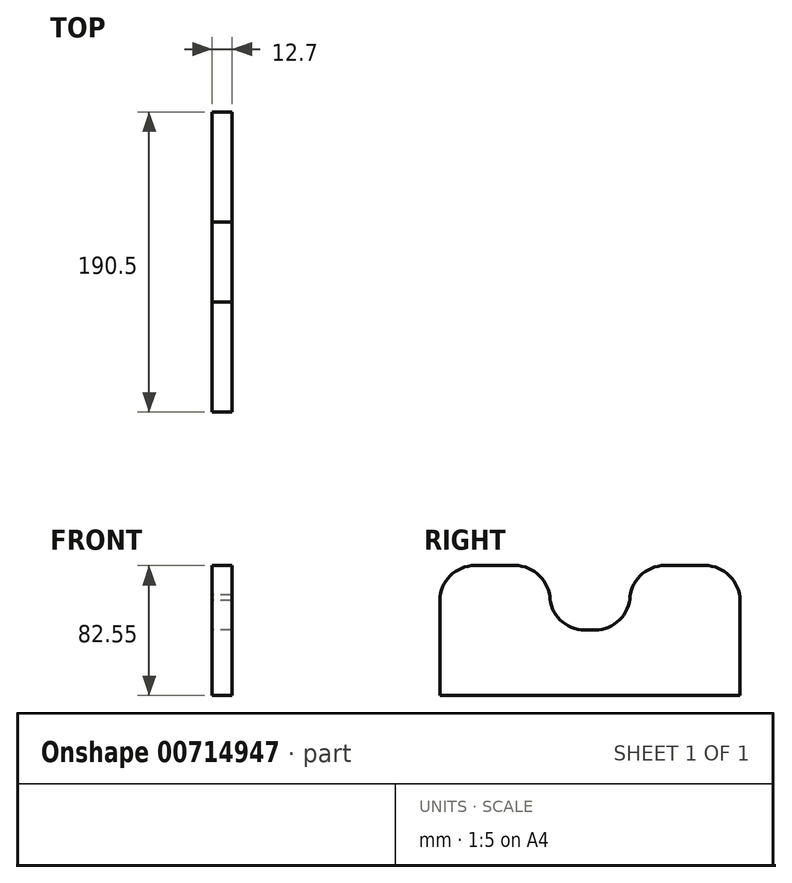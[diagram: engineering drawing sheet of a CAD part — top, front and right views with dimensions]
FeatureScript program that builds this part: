
annotation { "Feature Type Name" : "Feature", "Feature Type Description" : "" }
export const myFeature = defineFeature(function(context is Context, id is Id, definition is map)
    precondition{}
    {
        {
            var Q0;
            Q0=qCreatedBy(makeId("Right.planeOp"),FACE);
            var sketch = newSketch(context, id + "F0", { "sketchPlane" : qUnion([Q0])});
            skPoint(sketch, "E0.middle", {"position": v(0, 0) * mm});
            skLineSegment(sketch, "E1.top", {"start": v(-73.03, 88.9) * mm, "end": v(-47.63, 88.9) * mm});
            skLineSegment(sketch, "E1.left", {"start": v(-95.25, 6.35) * mm, "end": v(-95.25, 66.68) * mm});
            skLineSegment(sketch, "E1.right", {"start": v(95.25, 6.35) * mm, "end": v(95.25, 66.68) * mm});
            skPoint(sketch, "E0.bottom.end.orphan", {"position": v(-95.25, -6.35) * mm});
            skPoint(sketch, "E0.left.start.orphan", {"position": v(95.25, -6.35) * mm});
            skPoint(sketch, "E0.top.start.orphan", {"position": v(95.25, 6.35) * mm});
            skLineSegment(sketch, "E2", {"start": v(-95.25, 6.35) * mm, "end": v(95.25, 6.35) * mm});
            skLineSegment(sketch, "E3.top", {"start": v(-3.18, 47.86) * mm, "end": v(3.17, 47.86) * mm});
            skLineSegment(sketch, "E3.left", {"start": v(-25.4, 70.08) * mm, "end": v(-25.4, 66.67) * mm});
            skLineSegment(sketch, "E3.right", {"start": v(25.4, 70.08) * mm, "end": v(25.4, 66.68) * mm});
            skLineSegment(sketch, "E4.trimOffspring", {"start": v(47.62, 88.9) * mm, "end": v(73.02, 88.9) * mm});
            skPoint(sketch, "E5.visualSharp", {"position": v(-25.4, 47.86) * mm});
            skArc(sketch, "E5.filletArc", {"start": v(-25.4, 70.08) * mm, "mid": v(-18.9, 54.37) * mm, "end": v(-3.18, 47.86) * mm});
            skPoint(sketch, "E6.visualSharp", {"position": v(-25.4, 88.9) * mm});
            skArc(sketch, "E6.filletArc", {"start": v(-25.4, 66.67) * mm, "mid": v(-31.9, 82.4) * mm, "end": v(-47.63, 88.9) * mm});
            skPoint(sketch, "E7.visualSharp", {"position": v(-95.25, 88.9) * mm});
            skArc(sketch, "E7.filletArc", {"start": v(-73.03, 88.9) * mm, "mid": v(-88.74, 82.4) * mm, "end": v(-95.25, 66.68) * mm});
            skPoint(sketch, "E8.visualSharp", {"position": v(95.25, 88.9) * mm});
            skArc(sketch, "E8.filletArc", {"start": v(95.25, 66.68) * mm, "mid": v(88.74, 82.4) * mm, "end": v(73.02, 88.9) * mm});
            skPoint(sketch, "E9.visualSharp", {"position": v(25.4, 88.9) * mm});
            skArc(sketch, "E9.filletArc", {"start": v(47.62, 88.9) * mm, "mid": v(31.9, 82.4) * mm, "end": v(25.4, 66.68) * mm});
            skPoint(sketch, "E10.visualSharp", {"position": v(25.4, 47.86) * mm});
            skArc(sketch, "E10.filletArc", {"start": v(3.17, 47.86) * mm, "mid": v(18.9, 54.37) * mm, "end": v(25.4, 70.08) * mm});
            skSolve(sketch);
        }
        {
            var Q0;
            Q0 = qSketchRegion(id + "F0", true);
            extrude(context, id + "F1", {"entities" : qUnion([Q0]), "depth" : 12.7 * mm, "offsetDistance" : 25.4 * mm});
        }
    });
